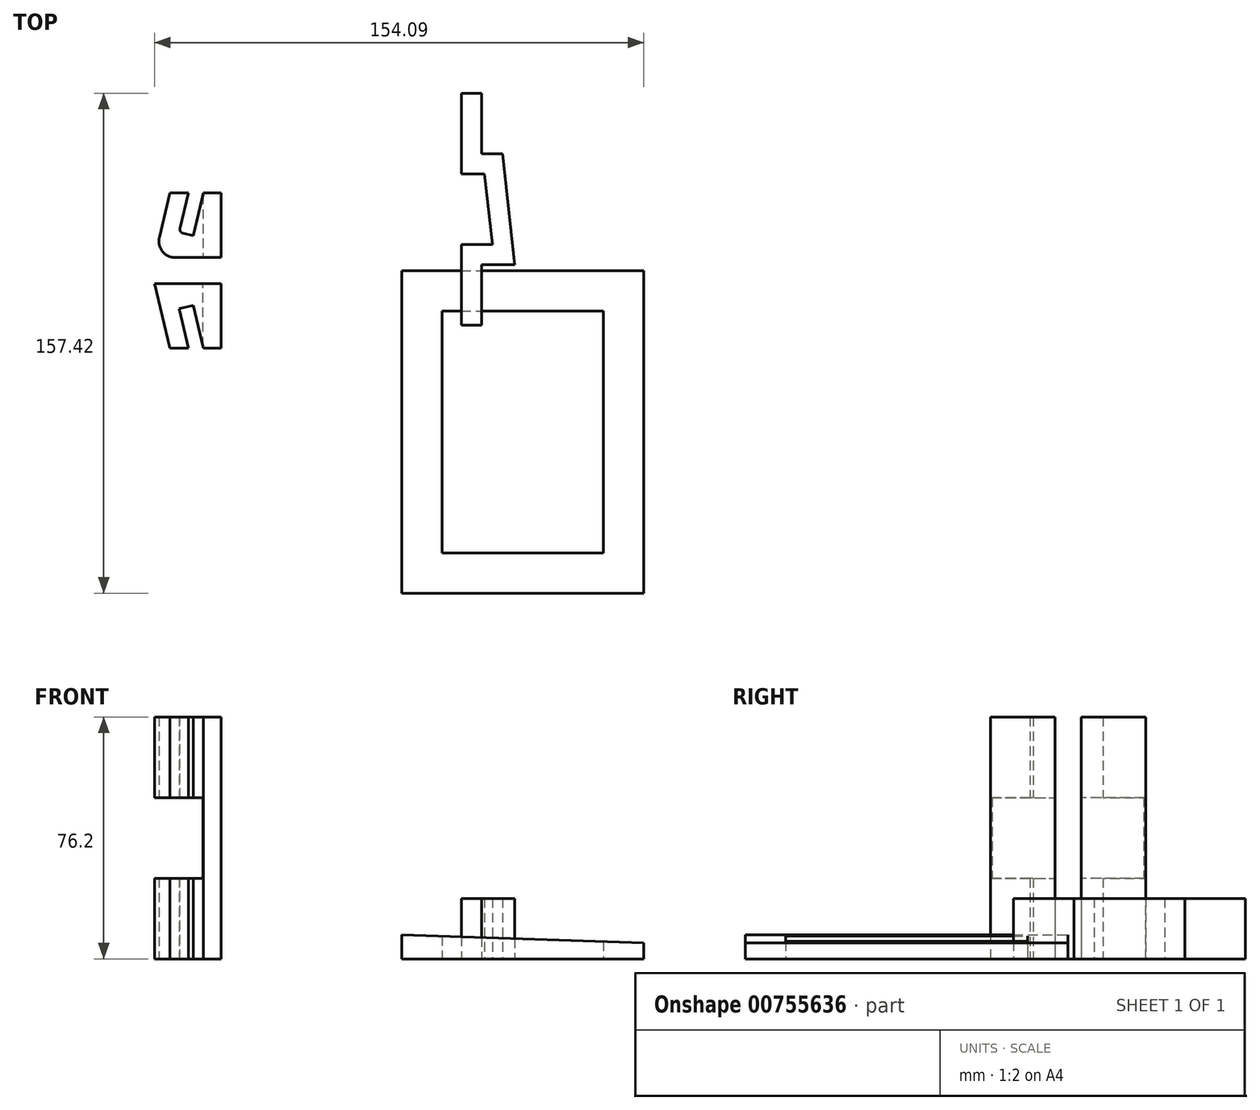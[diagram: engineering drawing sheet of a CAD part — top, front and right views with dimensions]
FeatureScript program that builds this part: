
annotation { "Feature Type Name" : "Feature", "Feature Type Description" : "" }
export const myFeature = defineFeature(function(context is Context, id is Id, definition is map)
    precondition{}
    {
        {
            var Q0;
            Q0=qCreatedBy(makeId("Front.planeOp"),FACE);
            var sketch = newSketch(context, id + "F0", { "sketchPlane" : qUnion([Q0])});
            skLineSegment(sketch, "E0.bottom", {"start": v(0, 0) * mm, "end": v(76.2, 0) * mm});
            skLineSegment(sketch, "E0.top", {"start": v(0, 7.62) * mm, "end": v(76.2, 5.08) * mm});
            skLineSegment(sketch, "E0.left", {"start": v(0, 0) * mm, "end": v(0, 7.62) * mm});
            skLineSegment(sketch, "E0.right", {"start": v(76.2, 0) * mm, "end": v(76.2, 5.08) * mm});
            skSolve(sketch);
        }
        {
            var Q0;
            Q0=makeQuery(id+"F0.imprint","IMPRINT",FACE,{"disambiguationData":[TD([[makeQuery(id+"F0.imprint","IMPRINT",EDGE,{"derivedFrom":sQuery(id+"F0.wireOp",EDGE,"E0.bottom")}),1.0]])]});
            extrude(context, id + "F1", {"entities" : qUnion([Q0]), "depth" : 101.6 * mm, "offsetDistance" : 25.4 * mm});
        }
        {
            var Q0;
            Q0=makeQuery(id+"F1.opExtrude","SWEPT_FACE",FACE,{"disambiguationData":[OSD([sQuery(id+"F0.wireOp",EDGE,"E0.bottom")])]});
            var sketch = newSketch(context, id + "F2", { "sketchPlane" : qUnion([Q0])});
            skLineSegment(sketch, "E1.bottom", {"start": v(63.5, 12.7) * mm, "end": v(12.7, 12.7) * mm});
            skLineSegment(sketch, "E1.top", {"start": v(63.5, 88.9) * mm, "end": v(12.7, 88.9) * mm});
            skLineSegment(sketch, "E1.left", {"start": v(63.5, 12.7) * mm, "end": v(63.5, 88.9) * mm});
            skLineSegment(sketch, "E1.right", {"start": v(12.7, 12.7) * mm, "end": v(12.7, 88.9) * mm});
            skLineSegment(sketch, "E2.0", {"start": v(0, 101.6) * mm, "end": v(0, 0) * mm, "construction": true});
            skLineSegment(sketch, "E3.0.1", {"start": v(76.2, 0) * mm, "end": v(76.2, 101.6) * mm, "construction": true});
            skLineSegment(sketch, "E4", {"start": v(76.2, 50.8) * mm, "end": v(0, 50.8) * mm, "construction": true});
            skLineSegment(sketch, "E5", {"start": v(38.1, 50.8) * mm, "end": v(38.1, 41.23) * mm, "construction": true});
            skSolve(sketch);
        }
        {
            var Q0;
            Q0=makeQuery(id+"F2.imprint","IMPRINT",FACE,{"disambiguationData":[TD([[makeQuery(id+"F2.imprint","IMPRINT",EDGE,{"derivedFrom":sQuery(id+"F2.wireOp",EDGE,"E1.bottom")}),-1.0]])]});
            extrude(context, id + "F3", {"entities" : qUnion([Q0]), "operationType" : NewBodyOperationType.REMOVE, "endBound" : BoundingType.THROUGH_ALL, "oppositeDirection" : true, "depth" : 25.4 * mm, "offsetDistance" : 25.4 * mm});
        }
        {
            var Q0;
            Q0=qCreatedBy(makeId("Top.planeOp"),FACE);
            var sketch = newSketch(context, id + "F4", { "sketchPlane" : qUnion([Q0])});
            skLineSegment(sketch, "E6", {"start": v(18.72, 55.82) * mm, "end": v(18.72, 30.42) * mm});
            skLineSegment(sketch, "E7", {"start": v(18.72, 30.42) * mm, "end": v(25.98, 30.42) * mm});
            skLineSegment(sketch, "E8", {"start": v(25.98, 30.42) * mm, "end": v(28.47, 8.17) * mm});
            skLineSegment(sketch, "E9", {"start": v(28.47, 8.17) * mm, "end": v(18.72, 8.17) * mm});
            skLineSegment(sketch, "E10", {"start": v(18.72, 8.17) * mm, "end": v(18.72, -17.23) * mm});
            skLineSegment(sketch, "E11", {"start": v(18.72, -17.23) * mm, "end": v(25.07, -17.23) * mm});
            skLineSegment(sketch, "E12", {"start": v(25.07, -17.23) * mm, "end": v(25.07, 1.82) * mm});
            skLineSegment(sketch, "E13", {"start": v(25.07, 1.82) * mm, "end": v(35.57, 1.82) * mm});
            skLineSegment(sketch, "E14", {"start": v(35.57, 1.82) * mm, "end": v(31.66, 36.77) * mm});
            skLineSegment(sketch, "E15", {"start": v(31.66, 36.77) * mm, "end": v(25.07, 36.77) * mm});
            skLineSegment(sketch, "E16", {"start": v(25.07, 36.77) * mm, "end": v(25.07, 55.82) * mm});
            skLineSegment(sketch, "E17", {"start": v(25.07, 55.82) * mm, "end": v(18.72, 55.82) * mm});
            skLineSegment(sketch, "E18", {"start": v(12.37, 11.35) * mm, "end": v(28.11, 11.35) * mm});
            skLineSegment(sketch, "E19", {"start": v(26.34, 27.25) * mm, "end": v(12.37, 27.25) * mm});
            skLineSegment(sketch, "E20", {"start": v(12.37, 27.25) * mm, "end": v(12.37, 11.35) * mm});
            skSolve(sketch);
        }
        {
            var Q0;
            Q0=makeQuery(id+"F4.imprint","IMPRINT",FACE,{"disambiguationData":[TD([[makeQuery(id+"F4.imprint","IMPRINT",EDGE,{"derivedFrom":sQuery(id+"F4.wireOp",EDGE,"E6")}),1.0]])]});
            extrude(context, id + "F5", {"entities" : qUnion([Q0]), "depth" : 19.05 * mm, "offsetDistance" : 25.4 * mm});
        }
        {
            var Q0;
            Q0=qCreatedBy(makeId("Top.planeOp"),FACE);
            var sketch = newSketch(context, id + "F6", { "sketchPlane" : qUnion([Q0])});
            skLineSegment(sketch, "E21", {"start": v(-45.6, 32.4) * mm, "end": v(-57.28, 32.4) * mm});
            skLineSegment(sketch, "E22", {"start": v(-57.28, 32.4) * mm, "end": v(-59.21, 40.56) * mm});
            skLineSegment(sketch, "E23", {"start": v(-50.83, -24.42) * mm, "end": v(-62, -24.42) * mm});
            skLineSegment(sketch, "E24", {"start": v(-62, -24.42) * mm, "end": v(-65.24, -10.83) * mm});
            skLineSegment(sketch, "E25", {"start": v(-69.69, -11.89) * mm, "end": v(-66.7, -24.42) * mm});
            skLineSegment(sketch, "E26", {"start": v(-66.7, -24.42) * mm, "end": v(-73.05, -24.42) * mm});
            skLineSegment(sketch, "E27", {"start": v(-73.05, -24.42) * mm, "end": v(-77.9, -4.1) * mm});
            skLineSegment(sketch, "E28", {"start": v(-77.9, -4.1) * mm, "end": v(-50.83, -4.1) * mm});
            skLineSegment(sketch, "E29", {"start": v(-50.83, -4.1) * mm, "end": v(-50.83, -24.42) * mm});
            skLineSegment(sketch, "E30", {"start": v(-65.24, -10.83) * mm, "end": v(-69.69, -11.89) * mm});
            skLineSegment(sketch, "E31", {"start": v(-56.92, -4.1) * mm, "end": v(-56.92, -24.42) * mm});
            skSolve(sketch);
        }
        {
            var Q0;
            {var subQ0=sQuery(id+"F6.wireOp",EDGE,"E24");Q0=makeQuery(id+"F6.imprint","IMPRINT",FACE,{"disambiguationData":[TD([[makeQuery(id+"F6.imprint","IMPRINT",EDGE,{"derivedFrom":subQ0}),-1.0]])]});}
            extrude(context, id + "F7", {"entities" : qUnion([Q0]), "depth" : 76.2 * mm, "offsetDistance" : 25.4 * mm});
        }
        {
            var Q0;
            Q0=makeQuery(id+"F7.opExtrude","SWEPT_FACE",FACE,{"disambiguationData":[OSD([sQuery(id+"F6.wireOp",EDGE,"E28")])]});
            var sketch = newSketch(context, id + "F8", { "sketchPlane" : qUnion([Q0])});
            skLineSegment(sketch, "E32.0", {"start": v(77.9, 76.2) * mm, "end": v(77.9, 0) * mm, "construction": true});
            skLineSegment(sketch, "E32.1", {"start": v(77.9, 0) * mm, "end": v(77.9, 76.2) * mm});
            skLineSegment(sketch, "E33", {"start": v(77.9, 38.1) * mm, "end": v(77.9, 38.1) * mm});
            skLineSegment(sketch, "E34.bottom", {"start": v(77.9, 25.4) * mm, "end": v(62.65, 25.4) * mm});
            skLineSegment(sketch, "E34.top", {"start": v(77.9, 50.8) * mm, "end": v(62.65, 50.8) * mm});
            skLineSegment(sketch, "E34.left", {"start": v(77.9, 50.8) * mm, "end": v(77.9, 25.4) * mm});
            skLineSegment(sketch, "E34.right", {"start": v(62.65, 25.4) * mm, "end": v(62.65, 50.8) * mm});
            skSolve(sketch);
        }
        {
            var Q0;
            {var subQ2=sQuery(id+"F6.wireOp",EDGE,"E24");Q0=makeQuery(id+"F13.boolean.opBoolean","SPLIT",FACE,{"disambiguationData":[TD([makeQuery(id+"F13.opExtrude","SWEPT_FACE",FACE,{"disambiguationData":[OSD([sQuery(id+"F8.wireOp",EDGE,"E34.top")])]})])],"derivedFrom":makeQuery(id+"F7.opExtrude","SWEPT_FACE",FACE,{"disambiguationData":[OSD([subQ2])]})});}
            extrude(context, id + "F9", {"entities" : qUnion([Q0]), "operationType" : NewBodyOperationType.ADD, "depth" : 0.5 * mm, "offsetDistance" : 25.4 * mm});
        }
        {
            var Q0;
            {var subQ2=sQuery(id+"F6.wireOp",EDGE,"E25");Q0=makeQuery(id+"F13.boolean.opBoolean","SPLIT",FACE,{"disambiguationData":[TD([makeQuery(id+"F13.opExtrude","SWEPT_FACE",FACE,{"disambiguationData":[OSD([sQuery(id+"F8.wireOp",EDGE,"E34.top")])]})])],"derivedFrom":makeQuery(id+"F7.opExtrude","SWEPT_FACE",FACE,{"disambiguationData":[OSD([subQ2])]})});}
            extrude(context, id + "F10", {"entities" : qUnion([Q0]), "operationType" : NewBodyOperationType.REMOVE, "oppositeDirection" : true, "depth" : 0.5 * mm, "offsetDistance" : 25.4 * mm});
        }
        {
            var Q0;
            {var subQ0=sQuery(id+"F8.wireOp",EDGE,"E34.top");Q0=makeQuery(id+"F9.boolean.opBoolean","MERGE",FACE,{"derivedFrom":[makeQuery(id+"F13.boolean.opBoolean","COPY",FACE,{"derivedFrom":makeQuery(id+"F13.opExtrude","SWEPT_FACE",FACE,{"disambiguationData":[OSD([subQ0])]})}),makeQuery(id+"F9.opExtrude","SWEPT_FACE",FACE,{"disambiguationData":[OSD([sQuery(id+"F6.wireOp",EDGE,"E24"),subQ0])]})]});}
            var sketch = newSketch(context, id + "F11", { "sketchPlane" : qUnion([Q0])});
            skLineSegment(sketch, "E35", {"start": v(-62, 24.42) * mm, "end": v(-63.3, 24.42) * mm});
            skLineSegment(sketch, "E36", {"start": v(-63.3, 24.42) * mm, "end": v(-62.5, 24.54) * mm});
            skLineSegment(sketch, "E37", {"start": v(-62.5, 24.54) * mm, "end": v(-62, 24.42) * mm});
            skSolve(sketch);
        }
        {
            var Q0;
            {var subQ0=sQuery(id+"F11.wireOp",EDGE,"E37");Q0=makeQuery(id+"F11.imprint","IMPRINT",FACE,{"disambiguationData":[TD([[makeQuery(id+"F11.imprint","IMPRINT",EDGE,{"derivedFrom":subQ0}),-1.0]])]});}
            var Q1;
            {var subQ0=sQuery(id+"F11.wireOp",EDGE,"E36");Q1=makeQuery(id+"F11.imprint","IMPRINT",FACE,{"disambiguationData":[TD([[makeQuery(id+"F11.imprint","IMPRINT",EDGE,{"derivedFrom":subQ0}),-1.0]])]});}
            extrude(context, id + "F12", {"entities" : qUnion([Q0, Q1]), "operationType" : NewBodyOperationType.REMOVE, "endBound" : BoundingType.THROUGH_ALL, "oppositeDirection" : true, "depth" : 25.4 * mm, "offsetDistance" : 25.4 * mm});
        }
        {
            var Q0;
            Q0=makeQuery(id+"F8.imprint","IMPRINT",FACE,{"disambiguationData":[TD([[makeQuery(id+"F8.imprint","IMPRINT",EDGE,{"derivedFrom":sQuery(id+"F8.wireOp",EDGE,"E34.bottom")}),-1.0]])]});
            extrude(context, id + "F13", {"entities" : qUnion([Q0]), "operationType" : NewBodyOperationType.REMOVE, "endBound" : BoundingType.THROUGH_ALL, "oppositeDirection" : true, "depth" : 25.4 * mm, "offsetDistance" : 25.4 * mm});
        }
        {
            var Q0;
            Q0=makeQuery(id+"F7.opExtrude","SWEPT_BODY",BODY,{"disambiguationData":[OSD([sQuery(id+"F6.wireOp",EDGE,"E23"),sQuery(id+"F6.wireOp",EDGE,"E24"),sQuery(id+"F6.wireOp",EDGE,"E25"),sQuery(id+"F6.wireOp",EDGE,"E26"),sQuery(id+"F6.wireOp",EDGE,"E27"),sQuery(id+"F6.wireOp",EDGE,"E28"),sQuery(id+"F6.wireOp",EDGE,"E29"),sQuery(id+"F6.wireOp",EDGE,"E30")])]});
            var Q1;
            Q1=qCreatedBy(makeId("Front.planeOp"),FACE);
            mirror(context, id + "F14", {"entities" : qUnion([Q0]), "mirrorPlane" : qUnion([Q1])});
        }
        {
            var Q0;
            {var subQ0=sQuery(id+"F6.wireOp",EDGE,"E28");var subQ1=sQuery(id+"F6.wireOp",EDGE,"E27");Q0=makeQuery(id+"F14.opPattern","COPY",EDGE,{"derivedFrom":makeQuery(id+"F13.boolean.opBoolean","SPLIT",EDGE,{"disambiguationData":[TD([makeQuery(id+"F13.opExtrude","SWEPT_FACE",FACE,{"disambiguationData":[OSD([sQuery(id+"F8.wireOp",EDGE,"E34.bottom")])]})])],"derivedFrom":makeQuery(id+"F7.opExtrude","SWEPT_EDGE",EDGE,{"disambiguationData":[OSD([subQ1,subQ0])]})}),"instanceName":"1"});}
            var Q1;
            {var subQ0=sQuery(id+"F6.wireOp",EDGE,"E28");var subQ1=sQuery(id+"F6.wireOp",EDGE,"E27");Q1=makeQuery(id+"F14.opPattern","COPY",EDGE,{"derivedFrom":makeQuery(id+"F13.boolean.opBoolean","SPLIT",EDGE,{"disambiguationData":[TD([makeQuery(id+"F13.opExtrude","SWEPT_FACE",FACE,{"disambiguationData":[OSD([sQuery(id+"F8.wireOp",EDGE,"E34.top")])]})])],"derivedFrom":makeQuery(id+"F7.opExtrude","SWEPT_EDGE",EDGE,{"disambiguationData":[OSD([subQ1,subQ0])]})}),"instanceName":"1"});}
            fillet(context, id + "F15", {"entities" : qUnion([Q0, Q1]), "radius" : 5.08 * mm, "tangentPropagation" : true, "allowEdgeOverflow" : false});
        }
        {
            var Q0;
            {var subQ0=sQuery(id+"F6.wireOp",EDGE,"E30");var subQ1=sQuery(id+"F6.wireOp",EDGE,"E24");Q0=makeQuery(id+"F14.opPattern","COPY",EDGE,{"derivedFrom":makeQuery(id+"F13.boolean.opBoolean","SPLIT",EDGE,{"disambiguationData":[TD([makeQuery(id+"F13.opExtrude","SWEPT_FACE",FACE,{"disambiguationData":[OSD([sQuery(id+"F8.wireOp",EDGE,"E34.bottom")])]})])],"derivedFrom":makeQuery(id+"F7.opExtrude","SWEPT_EDGE",EDGE,{"disambiguationData":[OSD([subQ1,subQ0])]})}),"instanceName":"1"});}
            var Q1;
            Q1=makeQuery(id+"F14.opPattern","COPY",EDGE,{"derivedFrom":makeQuery(id+"F9.opExtrude","CAP_EDGE",EDGE,{"disambiguationData":[OSD([sQuery(id+"F6.wireOp",EDGE,"E24"),sQuery(id+"F6.wireOp",EDGE,"E30")])],"isStart":false}),"instanceName":"1"});
            var Q2;
            {var subQ0=sQuery(id+"F6.wireOp",EDGE,"E30");var subQ1=sQuery(id+"F6.wireOp",EDGE,"E25");Q2=makeQuery(id+"F14.opPattern","COPY",EDGE,{"derivedFrom":makeQuery(id+"F13.boolean.opBoolean","SPLIT",EDGE,{"disambiguationData":[TD([makeQuery(id+"F13.opExtrude","SWEPT_FACE",FACE,{"disambiguationData":[OSD([sQuery(id+"F8.wireOp",EDGE,"E34.bottom")])]})])],"derivedFrom":makeQuery(id+"F7.opExtrude","SWEPT_EDGE",EDGE,{"disambiguationData":[OSD([subQ1,subQ0])]})}),"instanceName":"1"});}
            var Q3;
            Q3=makeQuery(id+"F14.opPattern","COPY",EDGE,{"derivedFrom":makeQuery(id+"F10.boolean.opBoolean","COPY",EDGE,{"derivedFrom":makeQuery(id+"F10.opExtrude","CAP_EDGE",EDGE,{"disambiguationData":[OSD([sQuery(id+"F6.wireOp",EDGE,"E25"),sQuery(id+"F6.wireOp",EDGE,"E30")])],"isStart":false})}),"instanceName":"1"});
            fillet(context, id + "F16", {"entities" : qUnion([Q0, Q1, Q2, Q3]), "radius" : 1.27 * mm, "tangentPropagation" : true, "allowEdgeOverflow" : false});
        }
    });
